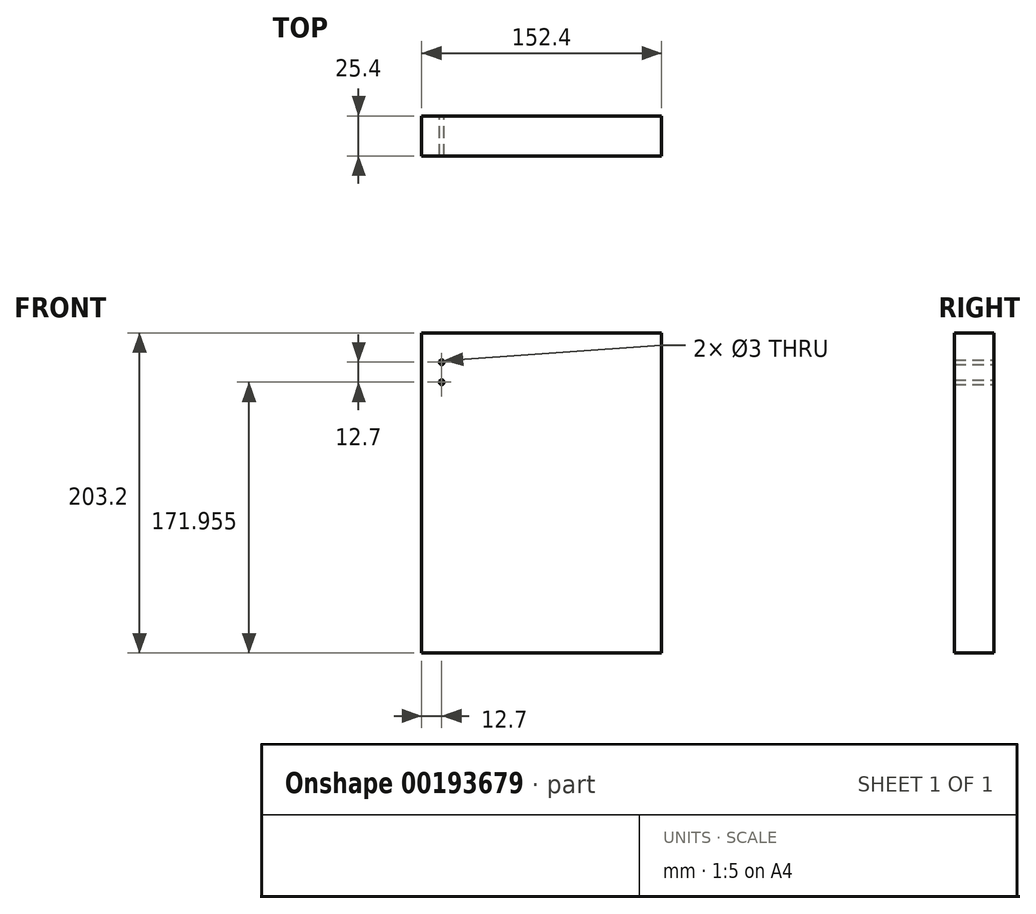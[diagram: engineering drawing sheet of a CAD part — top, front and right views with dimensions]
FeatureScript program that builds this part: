
annotation { "Feature Type Name" : "Feature", "Feature Type Description" : "" }
export const myFeature = defineFeature(function(context is Context, id is Id, definition is map)
    precondition{}
    {
        {
            var Q0;
            Q0=qCreatedBy(makeId("Front.planeOp"),FACE);
            var sketch = newSketch(context, id + "F0", { "sketchPlane" : qUnion([Q0])});
            skLineSegment(sketch, "E0.bottom", {"start": v(-76.2, -101.6) * mm, "end": v(76.2, -101.6) * mm});
            skLineSegment(sketch, "E0.top", {"start": v(-76.2, 101.6) * mm, "end": v(76.2, 101.6) * mm});
            skLineSegment(sketch, "E0.left", {"start": v(-76.2, -101.6) * mm, "end": v(-76.2, 101.6) * mm});
            skLineSegment(sketch, "E0.right", {"start": v(76.2, -101.6) * mm, "end": v(76.2, 101.6) * mm});
            skPoint(sketch, "E0.middle", {"position": v(0, 0) * mm});
            skSolve(sketch);
        }
        {
            var Q0;
            Q0=qCreatedBy(makeId("Front.planeOp"),FACE);
            var sketch = newSketch(context, id + "F1", { "sketchPlane" : qUnion([Q0])});
            skLineSegment(sketch, "E1", {"start": v(-63.5, 102.1) * mm, "end": v(-63.5, 83.06) * mm});
            skLineSegment(sketch, "E2", {"start": v(-63.5, 83.06) * mm, "end": v(-63.5, 70.36) * mm});
            skCircle(sketch, "E3", {"center": v(-63.5, 70.36) * mm, "radius": 1.5 * mm});
            skCircle(sketch, "E4", {"center": v(-63.5, 83.06) * mm, "radius": 1.5 * mm});
            skSolve(sketch);
        }
        {
            var Q0;
            Q0=makeQuery(id+"F0.imprint","IMPRINT",FACE,{"disambiguationData":[TD([[makeQuery(id+"F0.imprint","IMPRINT",EDGE,{"derivedFrom":sQuery(id+"F0.wireOp",EDGE,"E0.bottom")}),1.0]])]});
            extrude(context, id + "F2", {"entities" : qUnion([Q0]), "depth" : 25.4 * mm});
        }
        {
            var Q0;
            {var subQ0=sQuery(id+"F1.wireOp",EDGE,"E2");var subQ1=sQuery(id+"F1.wireOp",EDGE,"E1");var subQ2=makeQuery(id+"F1.imprint","INTERSECT",VERTEX,{"derivedFrom":[subQ1,subQ0]});Q0=makeQuery(id+"F1.imprint","IMPRINT",FACE,{"disambiguationData":[TD([[makeQuery(id+"F1.imprint","IMPRINT",EDGE,{"disambiguationData":[TD([[subQ2,1.0]])],"derivedFrom":subQ1}),-1.0]])]});}
            var Q1;
            {var subQ0=sQuery(id+"F1.wireOp",EDGE,"E2");var subQ1=sQuery(id+"F1.wireOp",EDGE,"E1");var subQ2=makeQuery(id+"F1.imprint","INTERSECT",VERTEX,{"derivedFrom":[subQ1,subQ0]});Q1=makeQuery(id+"F1.imprint","IMPRINT",FACE,{"disambiguationData":[TD([[makeQuery(id+"F1.imprint","IMPRINT",EDGE,{"disambiguationData":[TD([[subQ2,1.0]])],"derivedFrom":subQ1}),1.0]])]});}
            var Q2;
            Q2=makeQuery(id+"F1.imprint","IMPRINT",FACE,{"disambiguationData":[TD([[makeQuery(id+"F1.imprint","IMPRINT",EDGE,{"derivedFrom":sQuery(id+"F1.wireOp",EDGE,"E3")}),1.0]])]});
            extrude(context, id + "F3", {"entities" : qUnion([Q0, Q1, Q2]), "operationType" : NewBodyOperationType.REMOVE, "depth" : 25.4 * mm});
        }
    });
